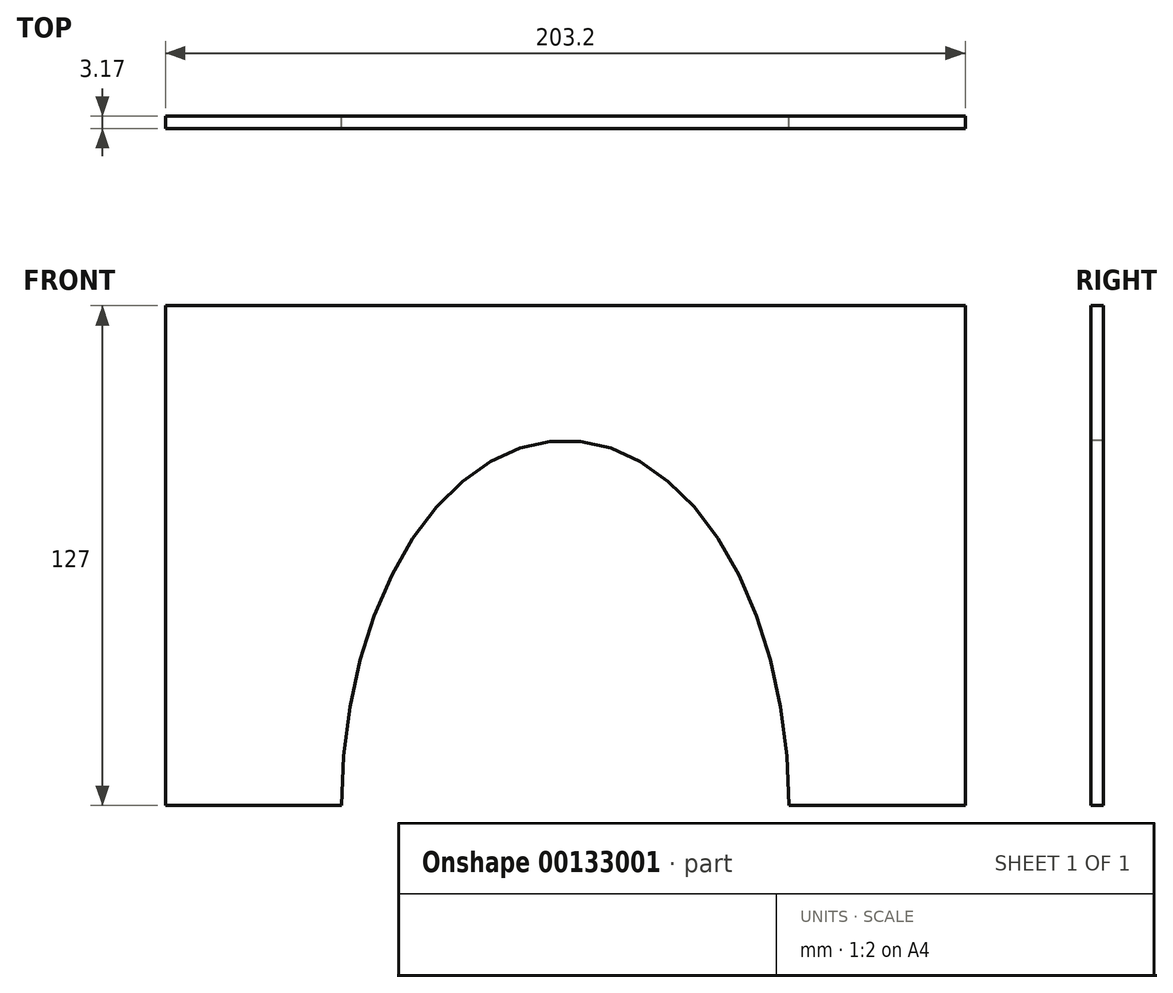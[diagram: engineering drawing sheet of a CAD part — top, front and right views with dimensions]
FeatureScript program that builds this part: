
annotation { "Feature Type Name" : "Feature", "Feature Type Description" : "" }
export const myFeature = defineFeature(function(context is Context, id is Id, definition is map)
    precondition{}
    {
        {
            var Q0;
            Q0=qCreatedBy(makeId("Front.planeOp"),FACE);
            var sketch = newSketch(context, id + "F0", { "sketchPlane" : qUnion([Q0])});
            skLineSegment(sketch, "E0.bottom", {"start": v(0, 0) * mm, "end": v(203.2, 0) * mm});
            skLineSegment(sketch, "E0.top", {"start": v(0, 127) * mm, "end": v(203.2, 127) * mm});
            skLineSegment(sketch, "E0.left", {"start": v(0, 0) * mm, "end": v(0, 127) * mm});
            skLineSegment(sketch, "E0.right", {"start": v(203.2, 0) * mm, "end": v(203.2, 127) * mm});
            skEllipticalArc(sketch, "E1", {});
            const initialGuessF0  = {"E1": [0.1016, 0, 0, 1, 0.09275809675455093, 0.05681710484477967, 4.71238898038469, 1.5707963267948966]};
            skSetInitialGuess(sketch, initialGuessF0);
            skSolve(sketch);
        }
        {
            var Q0;
            Q0=makeQuery(id+"F0.imprint","IMPRINT",FACE,{"disambiguationData":[TD([[makeQuery(id+"F0.imprint","IMPRINT",EDGE,{"derivedFrom":sQuery(id+"F0.wireOp",EDGE,"E0.top")}),-1.0]])]});
            extrude(context, id + "F1", {"entities" : qUnion([Q0]), "depth" : 3.17 * mm});
        }
    });
